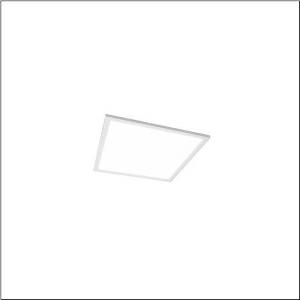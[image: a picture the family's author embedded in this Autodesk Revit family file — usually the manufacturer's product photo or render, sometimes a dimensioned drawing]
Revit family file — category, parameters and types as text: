
# Revit family: apollon_r__21_square_51mq13wd2313_d027
name_source: partatom
category: Lighting Fixtures
units: mm (PartAtom-declared; Revit-internal decimal feet)

## family parameters
Cut with Voids When Loaded = No
Host = Face
Light Source = No
Part Type = Normal
Room Calculation Point = No
Round Connector Dimension = Use Diameter
Shared = No

## types (1)
- Apollon® 21 square (1 x LED, 1700 lm, 15 W, 3000K)
    Apparent Load = 15 VA
    CIE Flux Codes = 59 88 97 100 100
    Color Rendering = 80
    Color Temperature = 3000K
    Default Elevation = 1800 mm
    Description = Apollon® 21 square, office luminaire, primary optical cover: micro prismatic cover, of PMMA, CAT 2 (L<= 3000cd/m²), light emission: direct distribution, primary light characteristic: symmetric, installation type: lay-in mounting, LED, rated luminous flux: 1.700lm, luminous efficacy: 113lm/W, light colour: 830, colour temperature: 3000K, control gear: ECG DALI, with terminal, 5-pole, mains connection: 220..240V, AC, 50/60Hz, rated input power: 15W, housing, of sheet steel, coated, pure white, length: 296mm, width: 296mm, height: 40mm, housing upper side, of sheet steel, galvanised, protection rating (complete): IP20, protection rating (lamp compartment, on room side): IP50, insulation class (complete): insulation class II (safety insulation), certification: CE, ENEC, permissible operating ambient temperature: -20..+40°C, packaging unit: 1 piece
    Height = 0 mm  [stored 0 ft]
    Lamp = 1 x LED
    Lamp Light Flux = 1700 lm
    Lamp Power = 15 W
    Lamp count = 1
    Length = 295 mm
    Luminous efficacy = 113 lm/W
    Manufacturer = Siteco
    ModVariant = No
    Model = 51MQ13WD2313
    Mounting Place = Ceiling
    Mounting Type = Recessed
    Number of Poles = 1
    OnlyDefault = Yes
    Power Factor = 1
    Product Name = Apollon® 21 square
    Product group = office luminaire | ceiling recessed
    ProductGroupID = 400
    Protection Class = Protection class II
    Protection Degree = IP 20
    RLX_Detail_Level = 1
    RlxData = <blob elided: 10737 chars, md5=e4365d5d>
    Socket = socket
    Standby Power = 0 W
    System Light Flux = 1700 lm
    System Power = 15 W
    Type Comments = Product without accessories
    Type Image = l_1006815.jpg
    URL = http://relux.com
    VarID = ---
    Voltage = 0 V
    Weight = 0.00 kg
    Width = 295 mm

note: [stored X ft] marks values corroborated as IEEE doubles in the binary element streams (Revit-internal decimal feet)

## geometry (parser evidence)
native form markers: Sweep x7
no freeform markers — native parametric forms only
